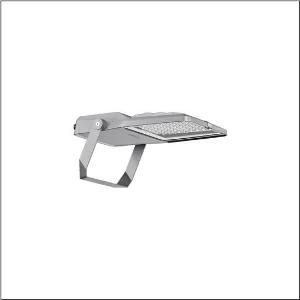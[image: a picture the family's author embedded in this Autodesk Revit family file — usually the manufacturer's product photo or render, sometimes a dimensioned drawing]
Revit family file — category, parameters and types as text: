
# Revit family: floodlight_fl_21_iq_mini___pl33t_5xa7772b1f1a_dd0a
name_source: partatom
category: Lighting Fixtures
units: mm (PartAtom-declared; Revit-internal decimal feet)

## family parameters
Cut with Voids When Loaded = No
Host = Face
Light Source = No
Part Type = Normal
Room Calculation Point = No
Round Connector Dimension = Use Diameter
Shared = No

## types (1)
- --- (1 x LED, 5110 lm, 45.5 W, 2200K)
    Apparent Load = 46 VA
    CIE Flux Codes = 26 75 99 100 100
    Color Rendering = 70
    Color Temperature = 2200K
    Default Elevation = 1800 mm
    Description = Floodlight FL 21 iQ mini, floodlight, primary light control with lens, of PMMA, primary optical cover: protective disc, of toughened safety glass, transparent, light distribution: PL33T, light emission: direct distribution, installation type: surface-mounted, lamps: LED, High Power LED, rated values: 5.110lm | 45,5W | 112,3lm/W (begin service life); end service life: 5.110lm | 48W; at 50% lumin. flux: 2.555lm | 21,4W | 119,4lm/W, colour temperature: 2200K, colour rendering: CRI > 70, light colour: 722, light setting 1 begin service life: 100% | 5.110lm | 45,5W | 112,3lm/W | 2.200K, light setting 1 end service life: 48W, further light settings possible, control: Street-Remote, Auto-Match, Temp-Guard, Night-Set, Smart-Wire, Desk-Remote (wireless, voltage-free reading and setting of iQ features in the workshop via application-optimized NFC function/RFID function), optimised constant luminous flux control (CLO 2.0), pre-setting: linear dimming characteristic, with terminal, 6-pole, mains connection: 220..240V, AC, 50/60Hz, luminaire housing, of diecast aluminium, powder-coated, SITECO metallic grey (DB 702S), corrosivity category C5 mid according to DIN EN ISO 12944suitable for swimming poolschlorine-resistant, sealing non-destructively replaceable, mounting bracket, of steel, galvanised, powder-coated, SITECO metallic grey (DB 702S), protection rating (complete): IP66, insulation class (complete): insulation class II (safety insulation), certification: CE, ENEC, VDE, protection symbol: D, impact resistance: IK08, permissible operating ambient temperature: -40..+40°C, permissible operating ambient temperature for outdoor applications: -40..+50°C, standard: DIN EN 12944, LABS conformity tested according to VDMA 24364:2018-05, packaging unit: 1 piece

Light Distribution: PL33T
    Height = 70 mm
    Lamp = 1 x LED
    Lamp Light Flux = 5110 lm
    Lamp Power = 45.5 W
    Lamp count = 1
    Length = 485 mm
    Luminous efficacy = 112 lm/W
    Manufacturer = Siteco
    ModVariant = No
    Model = 5XA7772B1F1A
    Mounting Place = Pole
    Mounting Type = Pole annexe
    Number of Poles = 1
    OnlyDefault = Yes
    Power Factor = 1
    Product Name = Floodlight FL 21 iQ mini | PL33T
    Product group = floodlight | pylon annexe
    ProductGroupID = 6201
    Protection Class = Protection class II
    Protection Degree = IP 66
    RLX_Detail_Level = 1
    RLX_Emergency_Light_Flux = 0 lm
    RLX_Emergency_Type = 0
    RLX_Emergency_Type_DB = No
    RlxData = <blob elided: 96401 chars, md5=662b9e4d>
    Socket = socket
    Standby Power = 0 W
    System Light Flux = 5110 lm
    System Power = 46 W
    Type Comments = factory setting: luminous flux: 100 % | dim-lin: 254 | 463 mA
    Type Image = l_1006845.jpg
    URL = http://relux.com
    VarID = @adj_151191
    Voltage = 0 V
    Weight = 0.00 kg
    Width = 337 mm

## geometry (parser evidence)
native form markers: Blend x4, Sweep x11
no freeform markers — native parametric forms only
